# Revit family: CEASF
name_source: partatom
category: Furniture
units: mm (PartAtom-declared; Revit-internal decimal feet)

## family parameters
Always vertical = Yes
Cut with Voids When Loaded = No
Enable Cutting in Views = No
OmniClass Number = 23.40.20.00
OmniClass Title = General Furniture and Specialties
Render Appearance Source = Family Geometry
Room Calculation Point = No
Shared = Yes
Work Plane-Based = No

## types (3) — shared parameters
Assembly Code = E2020200
Depth = 12 "
Description = Metal Frame - Wall shelving Unit
Manufacturer = Teknion
Manufacturer Fax = 416.661.4586
Model = CEASF
Product Documentation Link = http://www.teknion.com
http://www.teknion.com
Product Line = Expansion Casework +
Product Page URL = https://www.teknion.com
Series = Accesories
Sustainability Data = https://www.teknion.com
URL = www.teknion.com
Unit Weight URL = http://www.teknion.com
Warranty = http://www.teknion.com
Width = 0.625 "
zero-valued in all types: Default Elevation, Length

## per-type parameters (varying)
| type | Height | Part Number | Two | three |
| 1 High | 12 " | CEASF1 | No | No |
| 3 High | 34.752 " | CEASF3 | No | Yes |
| 2 High | 23.374 " | CEASF2 | Yes | No |

## geometry (parser evidence)
native form markers: Sweep x3
no freeform markers — native parametric forms only
